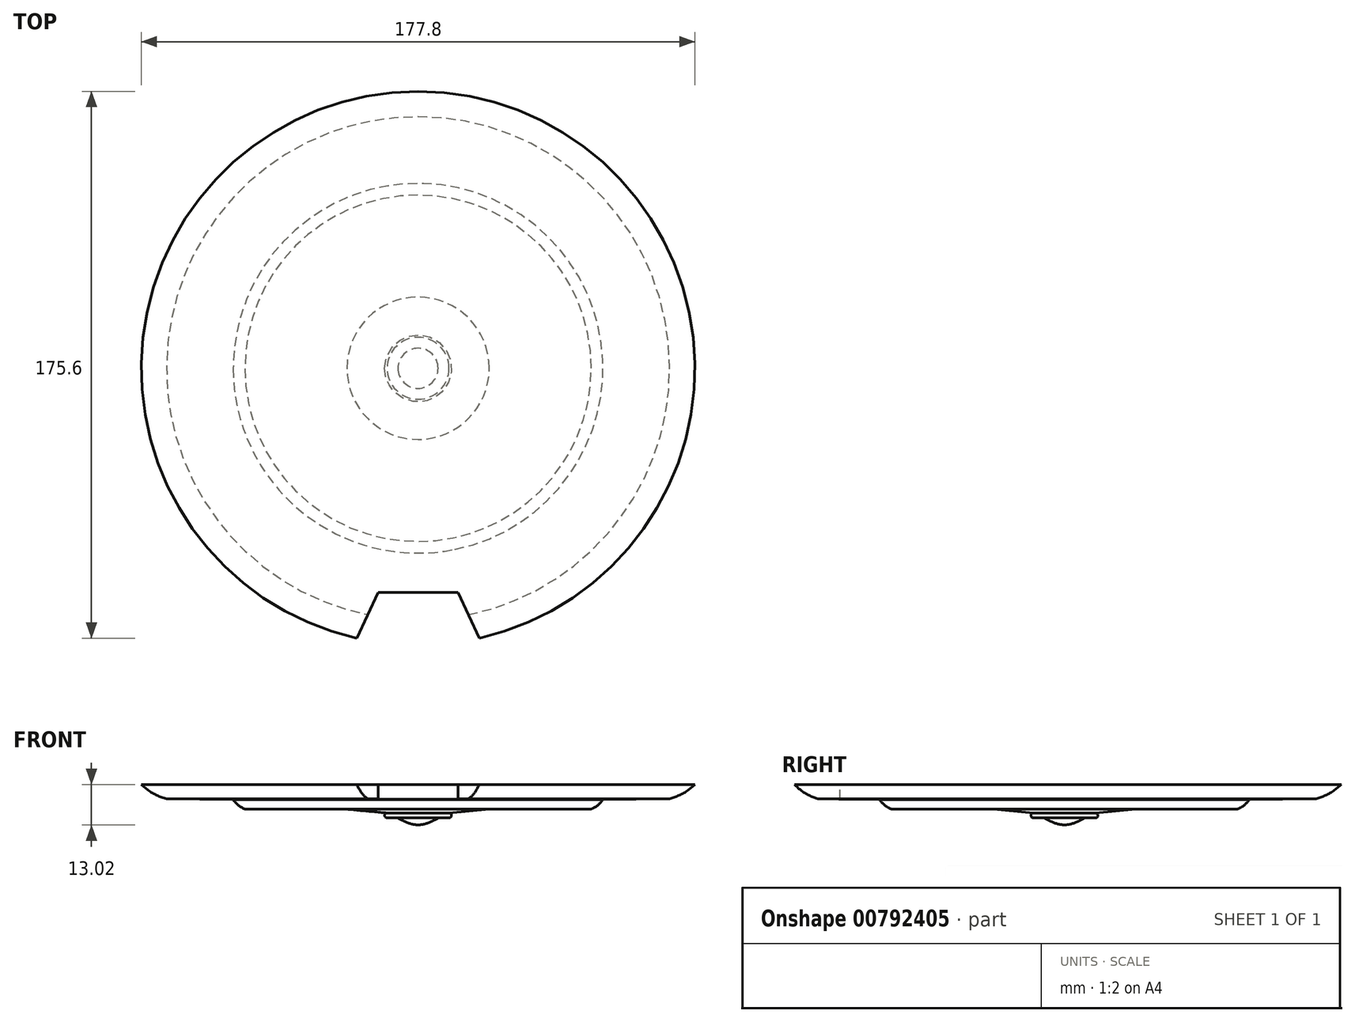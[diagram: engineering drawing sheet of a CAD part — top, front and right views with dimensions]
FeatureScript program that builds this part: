
annotation { "Feature Type Name" : "Feature", "Feature Type Description" : "" }
export const myFeature = defineFeature(function(context is Context, id is Id, definition is map)
    precondition{}
    {
        {
            var Q0;
            Q0=qCreatedBy(makeId("Front.planeOp"),FACE);
            var sketch = newSketch(context, id + "F0", { "sketchPlane" : qUnion([Q0])});
            skLineSegment(sketch, "E0", {"start": v(0, 0) * mm, "end": v(-88.9, 0) * mm});
            skLineSegment(sketch, "E1", {"start": v(0, 9.42) * mm, "end": v(0, 10.74) * mm});
            skLineSegment(sketch, "E2", {"start": v(0, 10.74) * mm, "end": v(0, 9.42) * mm});
            skPoint(sketch, "E3.orphan", {"position": v(-8.12, 9.42) * mm});
            skArc(sketch, "E4.MirrorCS", {"start": v(0, -13.02) * mm, "mid": v(-3.36, -12.28) * mm, "end": v(-6.44, -10.74) * mm});
            skLineSegment(sketch, "E5.MirrorCS", {"start": v(0, 0) * mm, "end": v(0, -13.02) * mm});
            skLineSegment(sketch, "E6.MirrorCS", {"start": v(-9.95, -10.74) * mm, "end": v(-6.44, -10.74) * mm});
            skArc(sketch, "E7.MirrorCS", {"start": v(-9.95, -10.74) * mm, "mid": v(-10.74, -9.94) * mm, "end": v(-9.95, -9.14) * mm});
            skLineSegment(sketch, "E8.MirrorCS", {"start": v(-22.86, -7.91) * mm, "end": v(-9.95, -9.14) * mm});
            skLineSegment(sketch, "E9.MirrorCS", {"start": v(-55.62, -7.91) * mm, "end": v(-22.86, -7.91) * mm});
            skArc(sketch, "E10.MirrorCS", {"start": v(-55.62, -7.91) * mm, "mid": v(-57.7, -6.65) * mm, "end": v(-59.37, -4.87) * mm});
            skLineSegment(sketch, "E11.MirrorCS", {"start": v(-80.8, -4.55) * mm, "end": v(-59.37, -4.87) * mm});
            skArc(sketch, "E12.MirrorCS", {"start": v(-80.8, -4.55) * mm, "mid": v(-85.15, -2.81) * mm, "end": v(-88.9, 0) * mm});
            skPoint(sketch, "E13.end.orphan", {"position": v(-6.44, 10.74) * mm});
            skPoint(sketch, "E14.end.orphan", {"position": v(-9.95, 9.14) * mm});
            skPoint(sketch, "E14.start.orphan", {"position": v(-9.95, 10.74) * mm});
            skPoint(sketch, "E15.orphan", {"position": v(0, 13.02) * mm});
            skPoint(sketch, "E16.end.orphan", {"position": v(-22.86, 7.91) * mm});
            skPoint(sketch, "E17.start.orphan", {"position": v(-55.62, 7.91) * mm});
            skPoint(sketch, "E18.end.orphan", {"position": v(-59.37, 4.87) * mm});
            skPoint(sketch, "E19.start.orphan", {"position": v(-80.8, 4.55) * mm});
            skSolve(sketch);
        }
        {
            var Q0;
            Q0=makeQuery(id+"F0.imprint","IMPRINT",FACE,{"disambiguationData":[TD([[makeQuery(id+"F0.imprint","IMPRINT",EDGE,{"derivedFrom":sQuery(id+"F0.wireOp",EDGE,"E0")}),1.0]])]});
            var Q1;
            Q1=sQuery(id+"F0.wireOp",EDGE,"E1");
            revolve(context, id + "F1", {"surfaceOperationType" : NewSurfaceOperationType.NEW, "entities" : qUnion([Q0]), "axis" : qUnion([Q1]), "revolveType" : RevolveType.FULL});
        }
        {
            var Q0;
            Q0=qCreatedBy(makeId("Top.planeOp"),FACE);
            var sketch = newSketch(context, id + "F2", { "sketchPlane" : qUnion([Q0])});
            skLineSegment(sketch, "E20", {"start": v(-21.21, -90.1) * mm, "end": v(-12.84, -72.02) * mm});
            skLineSegment(sketch, "E21", {"start": v(-12.84, -72.02) * mm, "end": v(0, -72.02) * mm});
            skLineSegment(sketch, "E22", {"start": v(0, -72.02) * mm, "end": v(0, -96.04) * mm});
            skLineSegment(sketch, "E23", {"start": v(0, -96.04) * mm, "end": v(-21.21, -90.1) * mm});
            skLineSegment(sketch, "E24.MirrorCS", {"start": v(12.84, -72.02) * mm, "end": v(0, -72.02) * mm});
            skLineSegment(sketch, "E25.MirrorCS", {"start": v(21.21, -90.1) * mm, "end": v(12.84, -72.02) * mm});
            skLineSegment(sketch, "E26.MirrorCS", {"start": v(0, -96.04) * mm, "end": v(21.21, -90.1) * mm});
            skSolve(sketch);
        }
        {
            var Q0;
            Q0 = qSketchRegion(id + "F2", true);
            extrude(context, id + "F3", {"entities" : qUnion([Q0]), "operationType" : NewBodyOperationType.REMOVE, "endBound" : BoundingType.SYMMETRIC, "oppositeDirection" : true, "depth" : 25.4 * mm, "offsetDistance" : 25.4 * mm});
        }
    });
